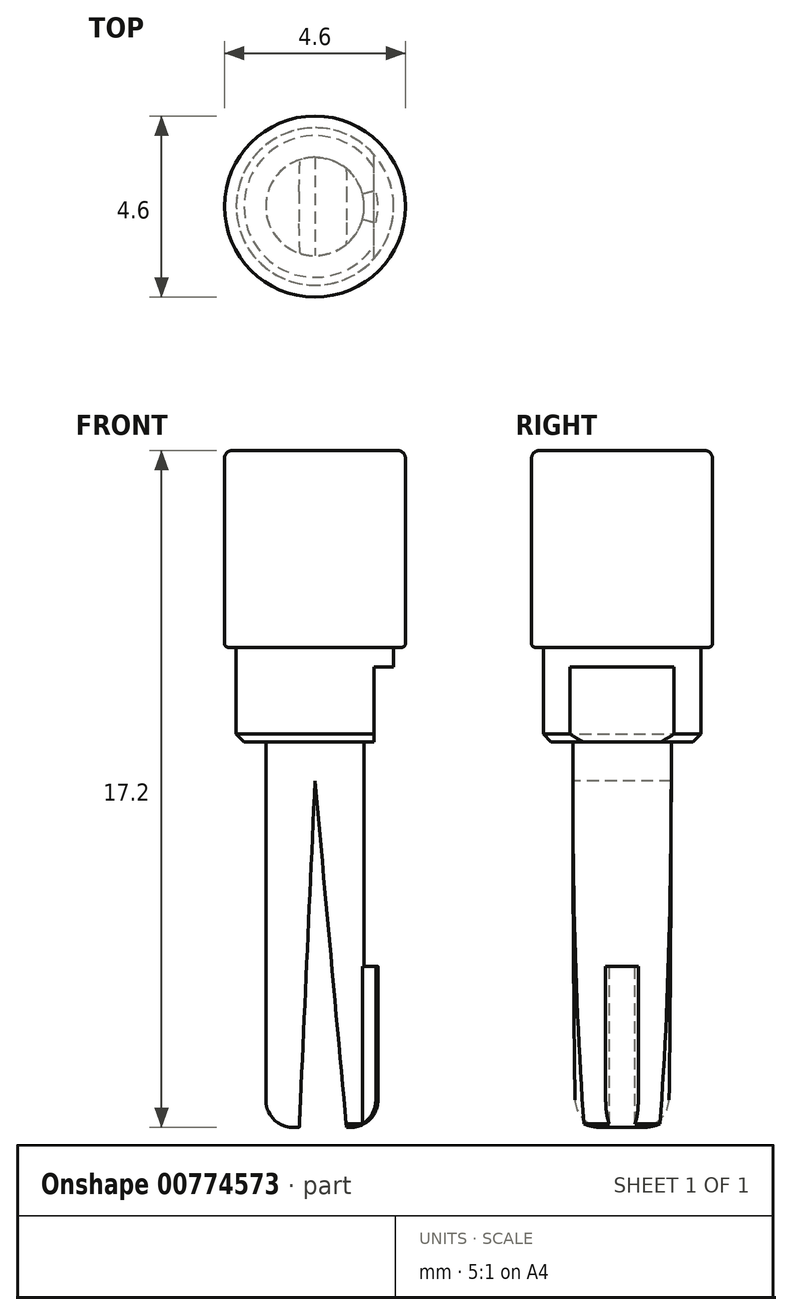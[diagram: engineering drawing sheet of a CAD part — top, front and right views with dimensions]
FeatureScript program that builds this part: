
annotation { "Feature Type Name" : "Feature", "Feature Type Description" : "" }
export const myFeature = defineFeature(function(context is Context, id is Id, definition is map)
    precondition{}
    {
        {
            var Q0;
            Q0=qCreatedBy(makeId("Front.planeOp"),FACE);
            var sketch = newSketch(context, id + "F0", { "sketchPlane" : qUnion([Q0])});
            skLineSegment(sketch, "E0", {"start": v(-2.3, 17.2) * mm, "end": v(0, 17.2) * mm});
            skLineSegment(sketch, "E1", {"start": v(-2.3, 17.2) * mm, "end": v(-2.3, 12.2) * mm});
            skLineSegment(sketch, "E2", {"start": v(-2.3, 12.2) * mm, "end": v(-2, 12.2) * mm});
            skLineSegment(sketch, "E3", {"start": v(-2, 12.2) * mm, "end": v(-2, 9.8) * mm});
            skLineSegment(sketch, "E4", {"start": v(-2, 9.8) * mm, "end": v(-1.25, 9.8) * mm});
            skLineSegment(sketch, "E5", {"start": v(-1.25, 9.8) * mm, "end": v(-1.25, 0) * mm});
            skLineSegment(sketch, "E6", {"start": v(-1.25, 0) * mm, "end": v(0, 0) * mm});
            skLineSegment(sketch, "E7", {"start": v(0, 17.2) * mm, "end": v(0, 0) * mm, "construction": true});
            skLineSegment(sketch, "E8", {"start": v(0, 17.2) * mm, "end": v(0, 0) * mm});
            skSolve(sketch);
        }
        {
            var Q0;
            Q0 = qSketchRegion(id + "F0", true);
            var Q1;
            Q1=sQuery(id+"F0.wireOp",EDGE,"E7");
            revolve(context, id + "F1", {"surfaceOperationType" : NewSurfaceOperationType.NEW, "entities" : qUnion([Q0]), "axis" : qUnion([Q1]), "revolveType" : RevolveType.FULL});
        }
        {
            var Q0;
            Q0=makeQuery(id+"F1.opRevolve","SWEPT_FACE",FACE,{"disambiguationData":[OSD([sQuery(id+"F0.wireOp",EDGE,"E4")])]});
            var sketch = newSketch(context, id + "F2", { "sketchPlane" : qUnion([Q0])});
            skLineSegment(sketch, "E9", {"start": v(1.5, 1.32) * mm, "end": v(1.5, -1.32) * mm});
            skArc(sketch, "E10", {"start": v(1.5, -1.32) * mm, "mid": v(2, 0) * mm, "end": v(1.5, 1.32) * mm});
            skSolve(sketch);
        }
        {
            var Q0;
            Q0=makeQuery(id+"F1.opRevolve","SWEPT_EDGE",EDGE,{"disambiguationData":[OSD([sQuery(id+"F0.wireOp",EDGE,"E0"),sQuery(id+"F0.wireOp",EDGE,"E1")])]});
            fillet(context, id + "F3", {"entities" : qUnion([Q0]), "radius" : 0.2 * mm, "tangentPropagation" : true, "allowEdgeOverflow" : false});
        }
        {
            var Q0;
            Q0=makeQuery(id+"F1.opRevolve","SWEPT_EDGE",EDGE,{"disambiguationData":[OSD([sQuery(id+"F0.wireOp",EDGE,"E1"),sQuery(id+"F0.wireOp",EDGE,"E2")])]});
            fillet(context, id + "F4", {"entities" : qUnion([Q0]), "radius" : 0.1 * mm, "tangentPropagation" : true, "allowEdgeOverflow" : false});
        }
        {
            var Q0;
            Q0=qCreatedBy(makeId("Front.planeOp"),FACE);
            var sketch = newSketch(context, id + "F5", { "sketchPlane" : qUnion([Q0])});
            skLineSegment(sketch, "E11", {"start": v(0, 8.8) * mm, "end": v(-0.4, 0) * mm});
            skLineSegment(sketch, "E12", {"start": v(0, 8.8) * mm, "end": v(0.8, 0) * mm});
            skLineSegment(sketch, "E13", {"start": v(-0.4, 0) * mm, "end": v(0.8, 0) * mm});
            skSolve(sketch);
        }
        {
            var Q0;
            Q0 = qSketchRegion(id + "F5", true);
            extrude(context, id + "F6", {"entities" : qUnion([Q0]), "operationType" : NewBodyOperationType.REMOVE, "endBound" : BoundingType.SYMMETRIC, "oppositeDirection" : true, "depth" : 25 * mm, "offsetDistance" : 25 * mm});
        }
        {
            var Q0;
            Q0=qCreatedBy(makeId("Front.planeOp"),FACE);
            var sketch = newSketch(context, id + "F7", { "sketchPlane" : qUnion([Q0])});
            skLineSegment(sketch, "E14", {"start": v(0, 0) * mm, "end": v(0, 3.63) * mm});
            skLineSegment(sketch, "E15.bottom", {"start": v(1.2, 4.1) * mm, "end": v(1.6, 4.1) * mm});
            skLineSegment(sketch, "E15.top", {"start": v(1.2, 0) * mm, "end": v(1.6, 0) * mm});
            skLineSegment(sketch, "E15.left", {"start": v(1.2, 4.1) * mm, "end": v(1.2, 0) * mm});
            skLineSegment(sketch, "E15.right", {"start": v(1.6, 4.1) * mm, "end": v(1.6, 0) * mm});
            skSolve(sketch);
        }
        {
            var Q0;
            Q0=makeQuery(id+"F7.imprint","IMPRINT",FACE,{"disambiguationData":[TD([[makeQuery(id+"F7.imprint","IMPRINT",EDGE,{"derivedFrom":sQuery(id+"F7.wireOp",EDGE,"E15.bottom")}),-1.0]])]});
            var Q1;
            Q1=sQuery(id+"F7.wireOp",EDGE,"E14");
            revolve(context, id + "F8", {"operationType" : NewBodyOperationType.ADD, "surfaceOperationType" : NewSurfaceOperationType.NEW, "entities" : qUnion([Q0]), "axis" : qUnion([Q1]), "revolveType" : RevolveType.TWO_DIRECTIONS, "angle" : 15 * degree, "angleBack" : 345 * degree});
        }
        {
            var Q0;
            {var subQ0=sQuery(id+"F0.wireOp",EDGE,"E5");var subQ1=sQuery(id+"F0.wireOp",EDGE,"E6");Q0=makeQuery(id+"F6.boolean.opBoolean","SPLIT",EDGE,{"disambiguationData":[TD([makeQuery(id+"F6.opExtrude","SWEPT_FACE",FACE,{"disambiguationData":[OSD([sQuery(id+"F5.wireOp",EDGE,"E11")])]})])],"derivedFrom":makeQuery(id+"F1.opRevolve","SWEPT_EDGE",EDGE,{"disambiguationData":[OSD([subQ0,subQ1])]})});}
            var Q1;
            Q1=makeQuery(id+"F8.opRevolve","SWEPT_EDGE",EDGE,{"disambiguationData":[OSD([sQuery(id+"F7.wireOp",EDGE,"E15.top"),sQuery(id+"F7.wireOp",EDGE,"E15.right")])]});
            fillet(context, id + "F9", {"entities" : qUnion([Q0, Q1]), "radius" : 0.7 * mm, "tangentPropagation" : true, "defaultsChanged" : true, "vertexSettings" : [], "allowEdgeOverflow" : false});
        }
        {
            var Q0;
            Q0=makeQuery(id+"F1.opRevolve","SWEPT_EDGE",EDGE,{"disambiguationData":[OSD([sQuery(id+"F0.wireOp",EDGE,"E3"),sQuery(id+"F0.wireOp",EDGE,"E4")])]});
            chamfer(context, id + "F10", {"entities" : qUnion([Q0]), "width" : 0.2 * mm, "tangentPropagation" : true});
        }
        {
            var Q0;
            Q0 = qSketchRegion(id + "F2", true);
            extrude(context, id + "F11", {"entities" : qUnion([Q0]), "operationType" : NewBodyOperationType.REMOVE, "oppositeDirection" : true, "depth" : 1.9 * mm, "offsetDistance" : 25 * mm});
        }
    });
